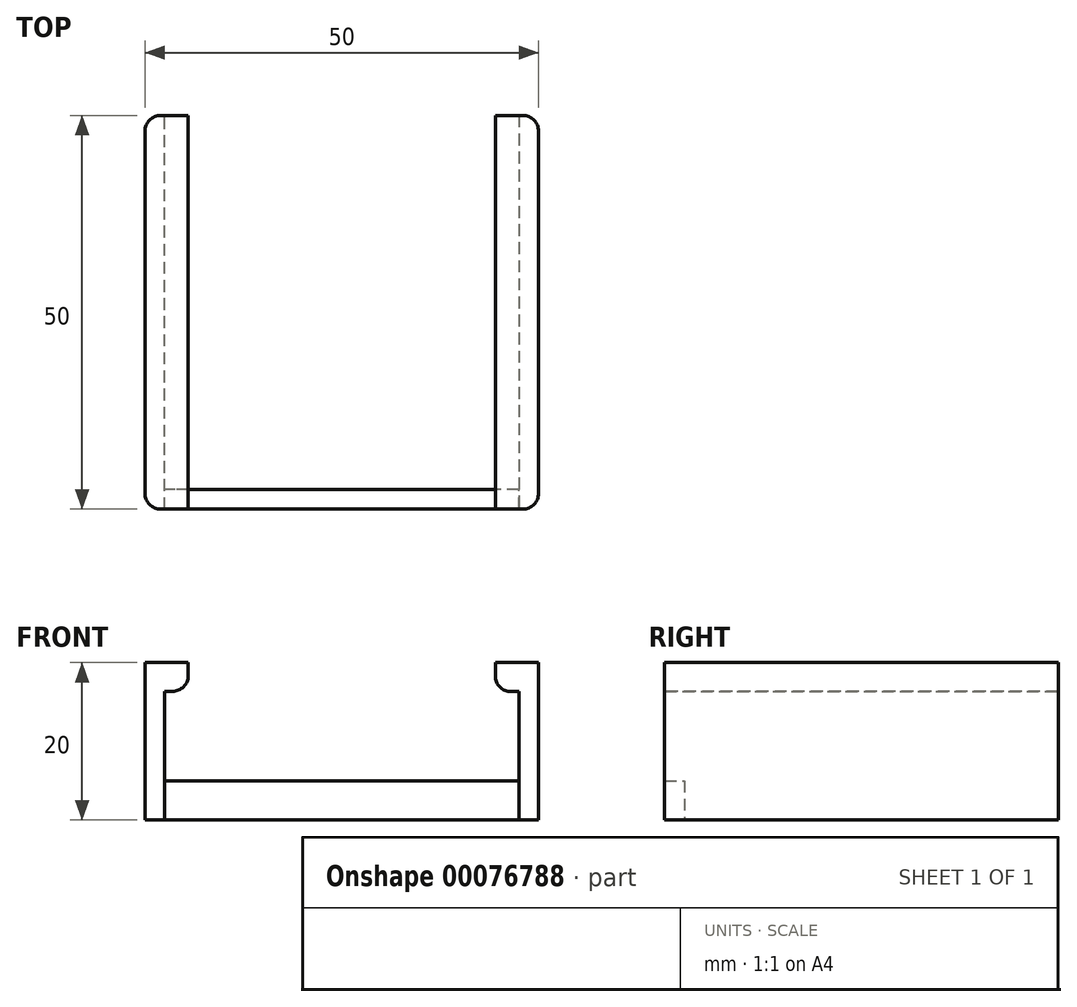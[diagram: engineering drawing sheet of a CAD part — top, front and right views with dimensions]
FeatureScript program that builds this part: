
annotation { "Feature Type Name" : "Feature", "Feature Type Description" : "" }
export const myFeature = defineFeature(function(context is Context, id is Id, definition is map)
    precondition{}
    {
        {
            var Q0;
            Q0=qCreatedBy(makeId("Top.planeOp"),FACE);
            var sketch = newSketch(context, id + "F0", { "sketchPlane" : qUnion([Q0])});
            skLineSegment(sketch, "E0", {"start": v(-41, 31.54) * mm, "end": v(-41, -18.46) * mm});
            skLineSegment(sketch, "E1", {"start": v(-41, -18.46) * mm, "end": v(-38.5, -18.46) * mm});
            skLineSegment(sketch, "E2", {"start": v(-38.5, -18.46) * mm, "end": v(-38.5, 31.54) * mm});
            skLineSegment(sketch, "E3", {"start": v(-38.5, 31.54) * mm, "end": v(-41, 31.54) * mm});
            skLineSegment(sketch, "E4", {"start": v(9, 31.54) * mm, "end": v(9, -18.46) * mm});
            skLineSegment(sketch, "E5", {"start": v(6.5, -18.46) * mm, "end": v(9, -18.46) * mm});
            skLineSegment(sketch, "E6", {"start": v(6.5, -18.46) * mm, "end": v(6.5, 31.54) * mm});
            skLineSegment(sketch, "E7", {"start": v(9, 31.54) * mm, "end": v(6.5, 31.54) * mm});
            skLineSegment(sketch, "E8", {"start": v(-38.5, -18.46) * mm, "end": v(6.5, -18.46) * mm});
            skLineSegment(sketch, "E9", {"start": v(6.5, -15.96) * mm, "end": v(-38.5, -15.96) * mm});
            skSolve(sketch);
        }
        {
            var Q0;
            Q0=makeQuery(id+"F0.imprint","IMPRINT",FACE,{"disambiguationData":[TD([[makeQuery(id+"F0.imprint","IMPRINT",EDGE,{"derivedFrom":sQuery(id+"F0.wireOp",EDGE,"E0")}),1.0]])]});
            var Q1;
            Q1=makeQuery(id+"F0.imprint","IMPRINT",FACE,{"disambiguationData":[TD([[makeQuery(id+"F0.imprint","IMPRINT",EDGE,{"derivedFrom":sQuery(id+"F0.wireOp",EDGE,"E4")}),-1.0]])]});
            extrude(context, id + "F1", {"entities" : qUnion([Q0, Q1]), "depth" : 20 * mm});
        }
        {
            var Q0;
            {var subQ0=sQuery(id+"F0.wireOp",EDGE,"E8");Q0=makeQuery(id+"F0.imprint","IMPRINT",FACE,{"disambiguationData":[TD([[makeQuery(id+"F0.imprint","IMPRINT",EDGE,{"derivedFrom":subQ0}),1.0]])]});}
            extrude(context, id + "F2", {"entities" : qUnion([Q0]), "depth" : 5 * mm});
        }
        {
            var Q0;
            Q0=makeQuery(id+"F1.opExtrude","SWEPT_FACE",FACE,{"disambiguationData":[OSD([sQuery(id+"F0.wireOp",EDGE,"E6")])]});
            var sketch = newSketch(context, id + "F3", { "sketchPlane" : qUnion([Q0])});
            skLineSegment(sketch, "E10", {"start": v(-31.54, 16.3) * mm, "end": v(18.46, 16.3) * mm});
            skLineSegment(sketch, "E11", {"start": v(18.46, 16.3) * mm, "end": v(18.46, 20) * mm});
            skLineSegment(sketch, "E12", {"start": v(18.46, 20) * mm, "end": v(-31.54, 20) * mm});
            skLineSegment(sketch, "E13", {"start": v(-31.54, 20) * mm, "end": v(-31.54, 16.3) * mm});
            skSolve(sketch);
        }
        {
            var Q0;
            Q0=makeQuery(id+"F3.imprint","IMPRINT",FACE,{"disambiguationData":[TD([[makeQuery(id+"F3.imprint","IMPRINT",EDGE,{"derivedFrom":sQuery(id+"F3.wireOp",EDGE,"E10")}),1.0]])]});
            extrude(context, id + "F4", {"entities" : qUnion([Q0]), "operationType" : NewBodyOperationType.ADD, "depth" : 3 * mm});
        }
        {
            var Q0;
            Q0=makeQuery(id+"F1.opExtrude","SWEPT_FACE",FACE,{"disambiguationData":[OSD([sQuery(id+"F0.wireOp",EDGE,"E2")])]});
            var sketch = newSketch(context, id + "F5", { "sketchPlane" : qUnion([Q0])});
            skLineSegment(sketch, "E14", {"start": v(-18.46, 16.35) * mm, "end": v(31.54, 16.35) * mm});
            skLineSegment(sketch, "E15", {"start": v(31.54, 16.35) * mm, "end": v(31.54, 20) * mm});
            skLineSegment(sketch, "E16", {"start": v(31.54, 20) * mm, "end": v(-18.46, 20) * mm});
            skLineSegment(sketch, "E17", {"start": v(-18.46, 20) * mm, "end": v(-18.46, 16.35) * mm});
            skSolve(sketch);
        }
        {
            var Q0;
            Q0=makeQuery(id+"F5.imprint","IMPRINT",FACE,{"disambiguationData":[TD([[makeQuery(id+"F5.imprint","IMPRINT",EDGE,{"derivedFrom":sQuery(id+"F5.wireOp",EDGE,"E14")}),1.0]])]});
            extrude(context, id + "F6", {"entities" : qUnion([Q0]), "operationType" : NewBodyOperationType.ADD, "depth" : 3 * mm});
        }
        {
            var Q0;
            Q0=makeQuery(id+"F4.opExtrude","CAP_EDGE",EDGE,{"disambiguationData":[OSD([sQuery(id+"F3.wireOp",EDGE,"E10")])],"isStart":false});
            var Q1;
            Q1=makeQuery(id+"F6.opExtrude","CAP_EDGE",EDGE,{"disambiguationData":[OSD([sQuery(id+"F5.wireOp",EDGE,"E14")])],"isStart":false});
            fillet(context, id + "F7", {"entities" : qUnion([Q0, Q1]), "radius" : 2 * mm, "tangentPropagation" : true, "allowEdgeOverflow" : false});
        }
        {
            var Q0;
            Q0=makeQuery(id+"F1.opExtrude","SWEPT_EDGE",EDGE,{"disambiguationData":[OSD([sQuery(id+"F0.wireOp",EDGE,"E0"),sQuery(id+"F0.wireOp",EDGE,"E1")])]});
            var Q1;
            Q1=makeQuery(id+"F1.opExtrude","SWEPT_EDGE",EDGE,{"disambiguationData":[OSD([sQuery(id+"F0.wireOp",EDGE,"E4"),sQuery(id+"F0.wireOp",EDGE,"E5")])]});
            var Q2;
            Q2=makeQuery(id+"F1.opExtrude","SWEPT_EDGE",EDGE,{"disambiguationData":[OSD([sQuery(id+"F0.wireOp",EDGE,"E4"),sQuery(id+"F0.wireOp",EDGE,"E7")])]});
            var Q3;
            Q3=makeQuery(id+"F1.opExtrude","SWEPT_EDGE",EDGE,{"disambiguationData":[OSD([sQuery(id+"F0.wireOp",EDGE,"E0"),sQuery(id+"F0.wireOp",EDGE,"E3")])]});
            fillet(context, id + "F8", {"entities" : qUnion([Q0, Q1, Q2, Q3]), "radius" : 2 * mm, "tangentPropagation" : true, "allowEdgeOverflow" : false});
        }
    });
